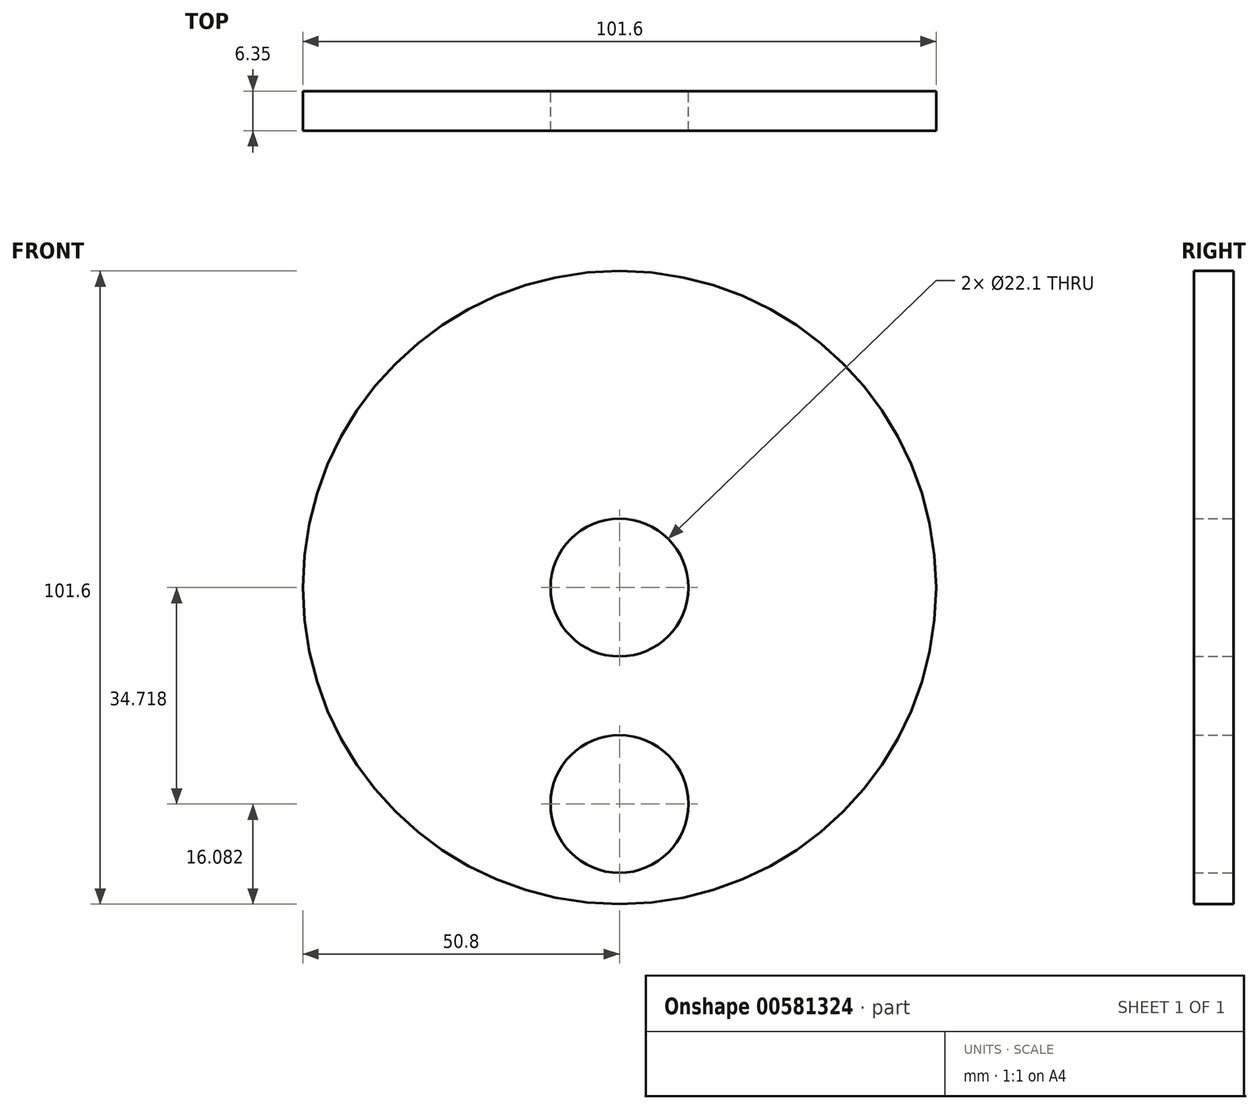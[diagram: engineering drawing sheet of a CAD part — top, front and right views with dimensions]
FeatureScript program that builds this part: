
annotation { "Feature Type Name" : "Feature", "Feature Type Description" : "" }
export const myFeature = defineFeature(function(context is Context, id is Id, definition is map)
    precondition{}
    {
        {
            var Q0;
            Q0=qCreatedBy(makeId("Front.planeOp"),FACE);
            var sketch = newSketch(context, id + "F0", { "sketchPlane" : qUnion([Q0])});
            skCircle(sketch, "E0", {"center": v(0, 0) * mm, "radius": 50.8 * mm});
            skSolve(sketch);
        }
        {
            var Q0;
            Q0=qCreatedBy(makeId("Front.planeOp"),FACE);
            var sketch = newSketch(context, id + "F1", { "sketchPlane" : qUnion([Q0])});
            skCircle(sketch, "E1", {"center": v(0, 0) * mm, "radius": 11.05 * mm});
            skSolve(sketch);
        }
        {
            var Q0;
            Q0=makeQuery(id+"F0.imprint","IMPRINT",FACE,{"disambiguationData":[TD([[makeQuery(id+"F0.imprint","IMPRINT",EDGE,{"derivedFrom":sQuery(id+"F0.wireOp",EDGE,"E0")}),1.0]])]});
            extrude(context, id + "F2", {"entities" : qUnion([Q0]), "depth" : 6.35 * mm, "offsetDistance" : 25.4 * mm});
        }
        {
            var Q0;
            Q0=makeQuery(id+"F1.imprint","IMPRINT",FACE,{"disambiguationData":[TD([[makeQuery(id+"F1.imprint","IMPRINT",EDGE,{"derivedFrom":sQuery(id+"F1.wireOp",EDGE,"E1")}),1.0]])]});
            extrude(context, id + "F3", {"entities" : qUnion([Q0]), "operationType" : NewBodyOperationType.REMOVE, "depth" : 10.4 * mm, "offsetDistance" : 25.4 * mm});
        }
        {
            var Q0;
            Q0=qCreatedBy(makeId("Front.planeOp"),FACE);
            var sketch = newSketch(context, id + "F4", { "sketchPlane" : qUnion([Q0])});
            skCircle(sketch, "E2", {"center": v(0, 0) * mm, "radius": 34.02 * mm});
            skSolve(sketch);
        }
        {
            var Q0;
            Q0=qCreatedBy(makeId("Front.planeOp"),FACE);
            var sketch = newSketch(context, id + "F5", { "sketchPlane" : qUnion([Q0])});
            skCircle(sketch, "E3", {"center": v(0, -34.72) * mm, "radius": 11.05 * mm});
            skSolve(sketch);
        }
        {
            var Q0;
            Q0=makeQuery(id+"F5.imprint","IMPRINT",FACE,{"disambiguationData":[TD([[makeQuery(id+"F5.imprint","IMPRINT",EDGE,{"derivedFrom":sQuery(id+"F5.wireOp",EDGE,"E3")}),1.0]])]});
            var Q1;
            Q1=makeQuery(id+"F1kClwGcosPIRbc_1.5.F5.imprint","IMPRINT",FACE,{"disambiguationData":[TD([[makeQuery(id+"F1kClwGcosPIRbc_1.5.F5.imprint","IMPRINT",EDGE,{"derivedFrom":sQuery(id+"F1kClwGcosPIRbc_1.5.F5.wireOp",EDGE,"E3")}),1.0]])]});
            var Q2;
            Q2=makeQuery(id+"F1kClwGcosPIRbc_1.4.F5.imprint","IMPRINT",FACE,{"disambiguationData":[TD([[makeQuery(id+"F1kClwGcosPIRbc_1.4.F5.imprint","IMPRINT",EDGE,{"derivedFrom":sQuery(id+"F1kClwGcosPIRbc_1.4.F5.wireOp",EDGE,"E3")}),1.0]])]});
            var Q3;
            Q3=makeQuery(id+"F1kClwGcosPIRbc_1.3.F5.imprint","IMPRINT",FACE,{"disambiguationData":[TD([[makeQuery(id+"F1kClwGcosPIRbc_1.3.F5.imprint","IMPRINT",EDGE,{"derivedFrom":sQuery(id+"F1kClwGcosPIRbc_1.3.F5.wireOp",EDGE,"E3")}),1.0]])]});
            var Q4;
            Q4=makeQuery(id+"F1kClwGcosPIRbc_1.2.F5.imprint","IMPRINT",FACE,{"disambiguationData":[TD([[makeQuery(id+"F1kClwGcosPIRbc_1.2.F5.imprint","IMPRINT",EDGE,{"derivedFrom":sQuery(id+"F1kClwGcosPIRbc_1.2.F5.wireOp",EDGE,"E3")}),1.0]])]});
            var Q5;
            Q5=makeQuery(id+"F1kClwGcosPIRbc_1.1.F5.imprint","IMPRINT",FACE,{"disambiguationData":[TD([[makeQuery(id+"F1kClwGcosPIRbc_1.1.F5.imprint","IMPRINT",EDGE,{"derivedFrom":sQuery(id+"F1kClwGcosPIRbc_1.1.F5.wireOp",EDGE,"E3")}),1.0]])]});
            extrude(context, id + "F6", {"entities" : qUnion([Q0, Q1, Q2, Q3, Q4, Q5]), "operationType" : NewBodyOperationType.REMOVE, "depth" : 6.35 * mm, "offsetDistance" : 25.4 * mm});
        }
    });
